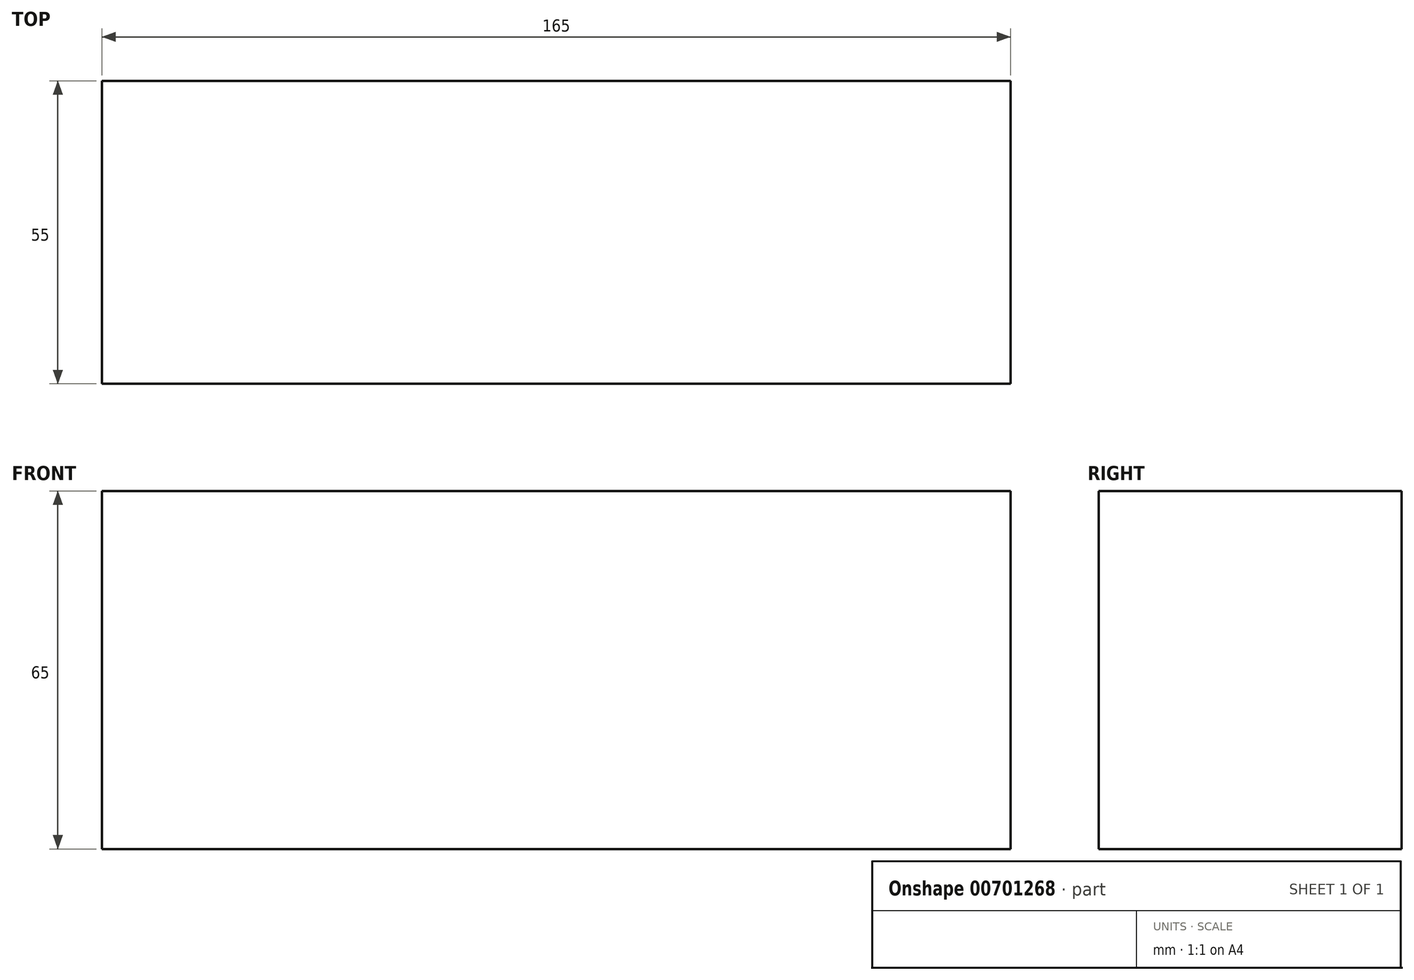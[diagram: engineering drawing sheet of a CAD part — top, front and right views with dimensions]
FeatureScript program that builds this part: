
annotation { "Feature Type Name" : "Feature", "Feature Type Description" : "" }
export const myFeature = defineFeature(function(context is Context, id is Id, definition is map)
    precondition{}
    {
        {
            var Q0;
            Q0=qCreatedBy(makeId("Top.planeOp"),FACE);
            var sketch = newSketch(context, id + "F0", { "sketchPlane" : qUnion([Q0])});
            skLineSegment(sketch, "E0.bottom", {"start": v(0, 0) * mm, "end": v(165, 0) * mm});
            skLineSegment(sketch, "E0.top", {"start": v(0, 55) * mm, "end": v(165, 55) * mm});
            skLineSegment(sketch, "E0.left", {"start": v(0, 0) * mm, "end": v(0, 55) * mm});
            skLineSegment(sketch, "E0.right", {"start": v(165, 0) * mm, "end": v(165, 55) * mm});
            skSolve(sketch);
        }
        {
            var Q0;
            Q0=makeQuery(id+"F0.imprint","IMPRINT",FACE,{"disambiguationData":[TD([[makeQuery(id+"F0.imprint","IMPRINT",EDGE,{"derivedFrom":sQuery(id+"F0.wireOp",EDGE,"E0.bottom")}),1.0]])]});
            extrude(context, id + "F1", {"entities" : qUnion([Q0]), "depth" : 65 * mm, "offsetDistance" : 25 * mm});
        }
    });
